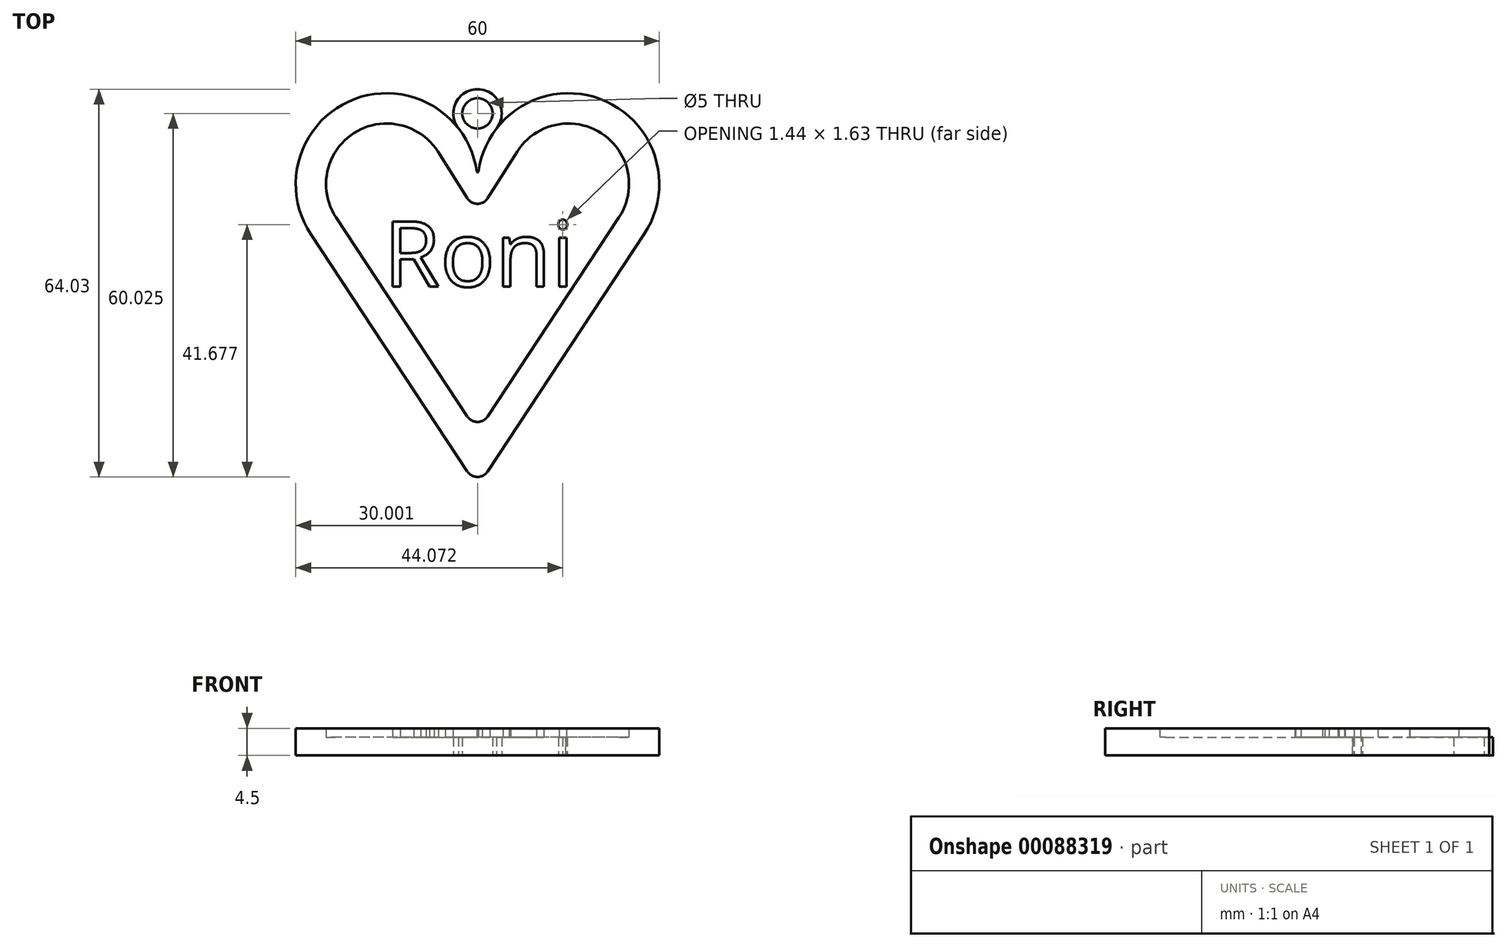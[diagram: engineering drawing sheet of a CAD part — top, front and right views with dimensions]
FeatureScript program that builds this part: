
annotation { "Feature Type Name" : "Feature", "Feature Type Description" : "" }
export const myFeature = defineFeature(function(context is Context, id is Id, definition is map)
    precondition{}
    {
        {
            var Q0;
            Q0=qCreatedBy(makeId("Top.planeOp"),FACE);
            var sketch = newSketch(context, id + "F0", { "sketchPlane" : qUnion([Q0])});
            skArc(sketch, "E0", {"start": v(-36.88, 22.56) * mm, "mid": v(-57, 34.65) * mm, "end": v(-64.27, 12.34) * mm});
            skArc(sketch, "E1", {"start": v(-9.23, 12.34) * mm, "mid": v(-16.5, 34.65) * mm, "end": v(-36.62, 22.56) * mm});
            skLineSegment(sketch, "E2", {"start": v(-64.27, 12.34) * mm, "end": v(-36.75, -29.4) * mm});
            skLineSegment(sketch, "E3", {"start": v(-36.75, -29.4) * mm, "end": v(-9.23, 12.34) * mm});
            skCircle(sketch, "E4", {"center": v(-36.75, 32.26) * mm, "radius": 4 * mm});
            skCircle(sketch, "E5", {"center": v(-36.75, 32.26) * mm, "radius": 2.5 * mm});
            skLineSegment(sketch, "E6.0", {"start": v(-60.1, 15.09) * mm, "end": v(-36.75, -20.32) * mm});
            skArc(sketch, "E7.0", {"start": v(-13.4, 15.09) * mm, "mid": v(-16.32, 29) * mm, "end": v(-30.2, 25.94) * mm});
            skArc(sketch, "E8.0", {"start": v(-43.3, 25.94) * mm, "mid": v(-57.18, 29) * mm, "end": v(-60.1, 15.09) * mm});
            skLineSegment(sketch, "E9.trimOffspring", {"start": v(-36.75, -20.32) * mm, "end": v(-13.4, 15.09) * mm});
            skText(sketch, "E10", { "text": "Roni", "fontName": "OpenSans-Regular.ttf"});
            skLineSegment(sketch, "E11", {"start": v(-36.75, 15.6) * mm, "end": v(-43.3, 25.94) * mm});
            skLineSegment(sketch, "E12", {"start": v(-36.75, 15.6) * mm, "end": v(-30.2, 25.94) * mm});
            skLineSegment(sketch, "E13", {"start": v(-36.88, 22.56) * mm, "end": v(-36.75, 22.5) * mm});
            skLineSegment(sketch, "E14", {"start": v(-36.62, 22.56) * mm, "end": v(-36.75, 22.5) * mm});
            skPoint(sketch, "E15.orphan", {"position": v(-36.75, 20.6) * mm});
            skPoint(sketch, "E16.orphan", {"position": v(-40.02, 20.77) * mm});
            skPoint(sketch, "E17.orphan", {"position": v(-33.47, 20.77) * mm});
            const initialGuessF0  = {"E10": [-0.05223, 0.00367, 1, 0, 0.01084]};
            skSetInitialGuess(sketch, initialGuessF0);
            skSolve(sketch);
        }
        {
            var Q0;
            Q0 = qSketchRegion(id + "F0", true);
            var Q1;
            Q1=makeQuery(id+"F0.imprint","IMPRINT",FACE,{"disambiguationData":[TD([[makeQuery(id+"F0.imprint","IMPRINT",EDGE,{"derivedFrom":sQuery(id+"F0.wireOp",EDGE,"E10.sketch_text.stroke-46")}),-1.0]])]});
            var Q2;
            {var subQ6=sQuery(id+"F0.wireOp",EDGE,"E2");Q2=makeQuery(id+"F0.imprint","IMPRINT",FACE,{"disambiguationData":[TD([[makeQuery(id+"F0.imprint","IMPRINT",EDGE,{"derivedFrom":subQ6}),1.0]])]});}
            var Q3;
            {var subQ0=sQuery(id+"F0.wireOp",EDGE,"E1");var subQ1=sQuery(id+"F0.wireOp",EDGE,"E0");var subQ2=makeQuery(id+"F0.imprint","INTERSECT",VERTEX,{"derivedFrom":[subQ1,subQ0]});Q3=makeQuery(id+"F0.imprint","IMPRINT",FACE,{"disambiguationData":[TD([[makeQuery(id+"F0.imprint","IMPRINT",EDGE,{"disambiguationData":[TD([[subQ2,-1.0]])],"derivedFrom":subQ1}),-1.0]])]});}
            var Q4;
            Q4=makeQuery(id+"F0.imprint","IMPRINT",FACE,{"disambiguationData":[TD([[makeQuery(id+"F0.imprint","IMPRINT",EDGE,{"derivedFrom":sQuery(id+"F0.wireOp",EDGE,"E5")}),-1.0]])]});
            var Q5;
            Q5=makeQuery(id+"F0.imprint","IMPRINT",FACE,{"disambiguationData":[TD([[makeQuery(id+"F0.imprint","IMPRINT",EDGE,{"derivedFrom":sQuery(id+"F0.wireOp",EDGE,"E6.0")}),1.0]])]});
            var Q6;
            Q6=makeQuery(id+"F0.imprint","IMPRINT",FACE,{"disambiguationData":[TD([[makeQuery(id+"F0.imprint","IMPRINT",EDGE,{"derivedFrom":sQuery(id+"F0.wireOp",EDGE,"E10.sketch_text.stroke-0")}),-1.0]])]});
            var Q7;
            Q7=makeQuery(id+"F0.imprint","IMPRINT",FACE,{"disambiguationData":[TD([[makeQuery(id+"F0.imprint","IMPRINT",EDGE,{"derivedFrom":sQuery(id+"F0.wireOp",EDGE,"E10.sketch_text.stroke-50")}),-1.0]])]});
            var Q8;
            Q8=makeQuery(id+"F0.imprint","IMPRINT",FACE,{"disambiguationData":[TD([[makeQuery(id+"F0.imprint","IMPRINT",EDGE,{"derivedFrom":sQuery(id+"F0.wireOp",EDGE,"E10.sketch_text.stroke-8")}),1.0]])]});
            var Q9;
            Q9=makeQuery(id+"F0.imprint","IMPRINT",FACE,{"disambiguationData":[TD([[makeQuery(id+"F0.imprint","IMPRINT",EDGE,{"derivedFrom":sQuery(id+"F0.wireOp",EDGE,"E10.sketch_text.stroke-16")}),-1.0]])]});
            var Q10;
            Q10=makeQuery(id+"F0.imprint","IMPRINT",FACE,{"disambiguationData":[TD([[makeQuery(id+"F0.imprint","IMPRINT",EDGE,{"derivedFrom":sQuery(id+"F0.wireOp",EDGE,"E10.sketch_text.stroke-33")}),-1.0]])]});
            var Q11;
            Q11=makeQuery(id+"F0.imprint","IMPRINT",FACE,{"disambiguationData":[TD([[makeQuery(id+"F0.imprint","IMPRINT",EDGE,{"derivedFrom":sQuery(id+"F0.wireOp",EDGE,"E10.sketch_text.stroke-11")}),1.0]])]});
            var Q12;
            Q12=makeQuery(id+"F0.imprint","IMPRINT",FACE,{"disambiguationData":[TD([[makeQuery(id+"F0.imprint","IMPRINT",EDGE,{"derivedFrom":sQuery(id+"F0.wireOp",EDGE,"E10.sketch_text.stroke-18")}),1.0]])]});
            var Q13;
            Q13=makeQuery(id+"F0.imprint","IMPRINT",FACE,{"disambiguationData":[TD([[makeQuery(id+"F0.imprint","IMPRINT",EDGE,{"derivedFrom":sQuery(id+"F0.wireOp",EDGE,"E10.sketch_text.stroke-44")}),1.0]])]});
            var Q14;
            Q14=makeQuery(id+"F0.imprint","IMPRINT",FACE,{"disambiguationData":[TD([[makeQuery(id+"F0.imprint","IMPRINT",EDGE,{"derivedFrom":sQuery(id+"F0.wireOp",EDGE,"E10.sketch_text.stroke-52")}),-1.0]])]});
            var Q15;
            Q15=makeQuery(id+"F0.imprint","IMPRINT",FACE,{"disambiguationData":[TD([[makeQuery(id+"F0.imprint","IMPRINT",EDGE,{"derivedFrom":sQuery(id+"F0.wireOp",EDGE,"E10.sketch_text.stroke-27")}),1.0]])]});
            extrude(context, id + "F1", {"entities" : qUnion([Q0, Q1, Q2, Q3, Q4, Q5, Q6, Q7, Q8, Q9, Q10, Q11, Q12, Q13, Q14, Q15]), "depth" : 3 * mm});
        }
        {
            var Q0;
            {var subQ6=sQuery(id+"F0.wireOp",EDGE,"E2");Q0=makeQuery(id+"F0.imprint","IMPRINT",FACE,{"disambiguationData":[TD([[makeQuery(id+"F0.imprint","IMPRINT",EDGE,{"derivedFrom":subQ6}),1.0]])]});}
            var Q1;
            Q1=makeQuery(id+"F0.imprint","IMPRINT",FACE,{"disambiguationData":[TD([[makeQuery(id+"F0.imprint","IMPRINT",EDGE,{"derivedFrom":sQuery(id+"F0.wireOp",EDGE,"E10.sketch_text.stroke-33")}),-1.0]])]});
            var Q2;
            Q2=makeQuery(id+"F0.imprint","IMPRINT",FACE,{"disambiguationData":[TD([[makeQuery(id+"F0.imprint","IMPRINT",EDGE,{"derivedFrom":sQuery(id+"F0.wireOp",EDGE,"E10.sketch_text.stroke-46")}),-1.0]])]});
            var Q3;
            Q3=makeQuery(id+"F0.imprint","IMPRINT",FACE,{"disambiguationData":[TD([[makeQuery(id+"F0.imprint","IMPRINT",EDGE,{"derivedFrom":sQuery(id+"F0.wireOp",EDGE,"E10.sketch_text.stroke-50")}),-1.0]])]});
            var Q4;
            Q4=makeQuery(id+"F0.imprint","IMPRINT",FACE,{"disambiguationData":[TD([[makeQuery(id+"F0.imprint","IMPRINT",EDGE,{"derivedFrom":sQuery(id+"F0.wireOp",EDGE,"E10.sketch_text.stroke-16")}),-1.0]])]});
            var Q5;
            Q5=makeQuery(id+"F0.imprint","IMPRINT",FACE,{"disambiguationData":[TD([[makeQuery(id+"F0.imprint","IMPRINT",EDGE,{"derivedFrom":sQuery(id+"F0.wireOp",EDGE,"E10.sketch_text.stroke-0")}),-1.0]])]});
            var Q6;
            Q6=makeQuery(id+"F0.imprint","IMPRINT",FACE,{"disambiguationData":[TD([[makeQuery(id+"F0.imprint","IMPRINT",EDGE,{"derivedFrom":sQuery(id+"F0.wireOp",EDGE,"E10.sketch_text.stroke-52")}),-1.0]])]});
            extrude(context, id + "F2", {"entities" : qUnion([Q0, Q1, Q2, Q3, Q4, Q5, Q6]), "operationType" : NewBodyOperationType.ADD, "depth" : 4.5 * mm});
        }
        {
            var Q0;
            {var subQ0=sQuery(id+"F0.wireOp",EDGE,"E3");var subQ1=sQuery(id+"F0.wireOp",EDGE,"E2");Q0=makeQuery(id+"F2.boolean.opBoolean","MERGE",EDGE,{"derivedFrom":[makeQuery(id+"F1.opExtrude","SWEPT_EDGE",EDGE,{"disambiguationData":[OSD([subQ1,subQ0])]}),makeQuery(id+"F2.opExtrude","SWEPT_EDGE",EDGE,{"disambiguationData":[OSD([subQ1,subQ0])]})]});}
            var Q1;
            Q1=makeQuery(id+"F2.opExtrude","SWEPT_EDGE",EDGE,{"disambiguationData":[OSD([sQuery(id+"F0.wireOp",EDGE,"E6.0"),sQuery(id+"F0.wireOp",EDGE,"E9.trimOffspring")])]});
            var Q2;
            Q2=makeQuery(id+"F2.opExtrude","SWEPT_EDGE",EDGE,{"disambiguationData":[OSD([sQuery(id+"F0.wireOp",EDGE,"E11"),sQuery(id+"F0.wireOp",EDGE,"E12")])]});
            fillet(context, id + "F3", {"entities" : qUnion([Q0, Q1, Q2]), "radius" : 2 * mm, "tangentPropagation" : true, "allowEdgeOverflow" : false});
        }
    });
